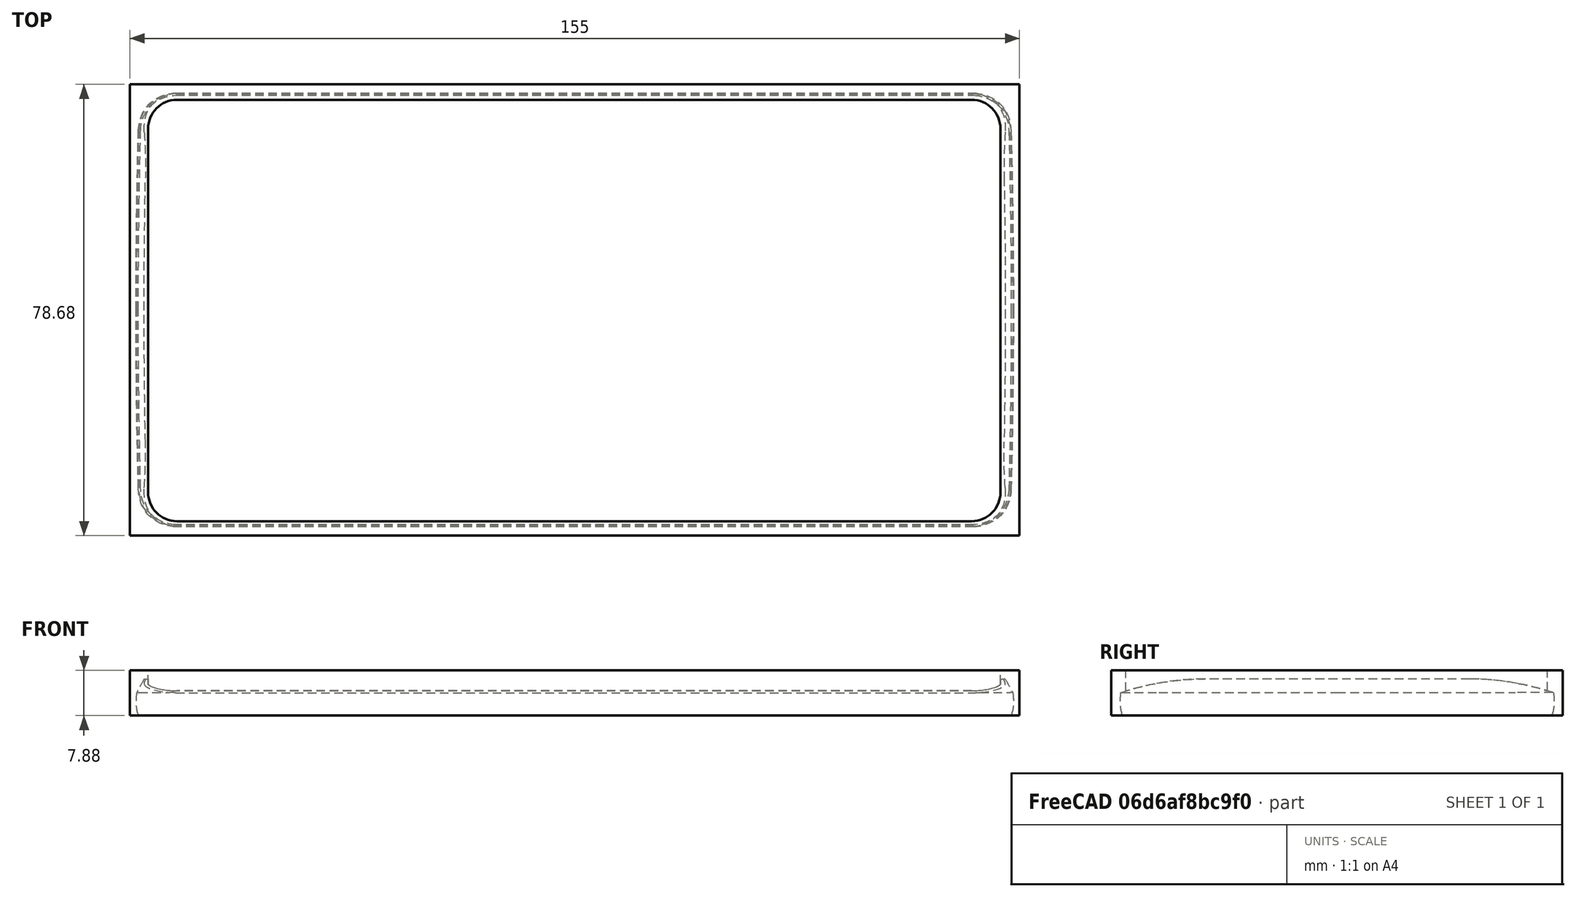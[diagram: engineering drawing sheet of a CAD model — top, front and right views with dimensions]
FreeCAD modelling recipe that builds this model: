
FCSTD DOCUMENT  (FreeCAD 0.18R13728 (Git))
Label: test109_opcase
License: All rights reserved
LicenseURL: http://en.wikipedia.org/wiki/All_rights_reserved
objects: Sketcher::SketchObject×2, Part::Extrusion×2, Part::Cut×2, Part::Feature×1, Mesh::Feature×1
note: 7 computed .brp shape members not serialized (recipe doc carries the construction recipe); baked Part::Feature solids carry a one-line shape summary decoded from their .brp

FEATURE [Sketcher::SketchObject] Sketch001
  MapMode = 5
  Placement = pos=(0,0,0) rot=(-0.57735,0.57735,0.57735;4.18879rad)
  sketch-geometry (16):
    g0: LineSegment [constr] StartX=-75.75 StartY=7.75 StartZ=0 EndX=0 EndY=7.75 EndZ=0
    g1: LineSegment [constr] StartX=0 StartY=7.75 StartZ=0 EndX=0 EndY=0 EndZ=0
    g2: LineSegment [constr] StartX=0 StartY=0 StartZ=0 EndX=-75.75 EndY=0 EndZ=0
    g3: LineSegment [constr] StartX=-75.75 StartY=0 StartZ=0 EndX=-75.75 EndY=7.75 EndZ=0
    g4: LineSegment [constr] StartX=-75.75 StartY=9.25 StartZ=0 EndX=0 EndY=9.25 EndZ=0
    g5: LineSegment [constr] StartX=1.5 StartY=7.75 StartZ=0 EndX=1.5 EndY=0 EndZ=0
    g6: LineSegment [constr] StartX=0 StartY=-1.5 StartZ=0 EndX=-75.75 EndY=-1.5 EndZ=0
    g7: LineSegment [constr] StartX=-77.25 StartY=0 StartZ=0 EndX=-77.25 EndY=7.75 EndZ=0
    g8: ArcOfCircle [constr] CenterX=0 CenterY=7.75 CenterZ=0 NormalX=0 NormalY=0 NormalZ=1 AngleXU=0 Radius=1.5 StartAngle=0 EndAngle=1.5708
    g9: ArcOfCircle [constr] CenterX=0 CenterY=0 CenterZ=0 NormalX=0 NormalY=0 NormalZ=1 AngleXU=0 Radius=1.5 StartAngle=4.71239 EndAngle=6.28319
    g10: ArcOfCircle [constr] CenterX=-75.75 CenterY=0 CenterZ=0 NormalX=0 NormalY=0 NormalZ=1 AngleXU=0 Radius=1.5 StartAngle=3.14159 EndAngle=4.71239
    g11: ArcOfCircle [constr] CenterX=-75.75 CenterY=7.75 CenterZ=0 NormalX=0 NormalY=0 NormalZ=1 AngleXU=0 Radius=1.5 StartAngle=1.5708 EndAngle=3.14159
    g12: LineSegment StartX=-77.2083 StartY=9.25 StartZ=0 EndX=1.47494 EndY=9.25 EndZ=0
    g13: LineSegment StartX=1.47494 StartY=9.25 StartZ=0 EndX=1.47494 EndY=1.36886 EndZ=0
    g14: LineSegment StartX=1.47494 StartY=1.36886 StartZ=0 EndX=-77.2083 EndY=1.36886 EndZ=0
    g15: LineSegment StartX=-77.2083 StartY=1.36886 StartZ=0 EndX=-77.2083 EndY=9.25 EndZ=0
  constraints (38):
    c: Coincident(g0,g1)
    c: Coincident(g1,g2)
    c: Coincident(g2,g3)
    c: Coincident(g3,g0)
    c: Horizontal(g0)
    c: Horizontal(g2)
    c: Vertical(g1)
    c: Vertical(g3)
    c: Coincident(g1,g-1)
    c: Horizontal(g4)
    c: Horizontal(g6)
    c: Vertical(g5)
    c: Vertical(g7)
    c: Tangent(g4,g8) = 1.5708
    c: Tangent(g5,g8) = 1.5708
    c: Tangent(g5,g9) = 1.5708
    c: Tangent(g6,g9) = 1.5708
    c: Tangent(g6,g10) = 1.5708
    c: Tangent(g7,g10) = 1.5708
    c: Tangent(g7,g11) = 1.5708
    c: Tangent(g4,g11) = 1.5708
    c: Radius(g11) = 1.5
    c: Equal(g11,g8)
    c: Equal(g11,g9)
    c: Equal(g11,g10)
    c: Coincident(g9,g-1)
    c: Coincident(g0,g11)
    c: PointOnObject(g12,g4)
    c: Horizontal(g12)
    c: Coincident(g12,g13)
    c: Vertical(g13)
    c: Coincident(g13,g14)
    c: Horizontal(g14)
    c: Coincident(g14,g15)
    c: Coincident(g15,g12)
    c: Vertical(g15)
    c: DistanceX(g0) = -75.75
    c: DistanceY(g0) = 7.75
FEATURE [Part::Extrusion] Extrude
  Base = -> Sketch001
  Dir = (-1,0,0)
  DirMode = 2
  FaceMakerClass = Part::FaceMakerBullseye
  LengthFwd = 155
  LengthRev = 0
  Placement = pos=(-1,0,0) rot=(0,0,1;0rad)
  Reversed = true
  Solid = true
  Symmetric = false
FEATURE [Part::Feature] test108_op3base
  shape: bbox 153.3 x 76.01 x 7.75 mm, 74 faces (baked)
FEATURE [Part::Cut] Cut
  Base = -> Extrude
  Tool = -> test108_op3base
FEATURE [Sketcher::SketchObject] Sketch
  MapMode = 5
  Placement = pos=(0,0,1.36886) rot=(1,0,0;3.14159rad)
  Support = -> [Cut]
  sketch-geometry (8):
    g0: LineSegment StartX=7.16177 StartY=-1.04562 StartZ=0 EndX=145.686 EndY=-1.04562 EndZ=0
    g1: LineSegment StartX=150.686 StartY=-6.04562 StartZ=0 EndX=150.686 EndY=-69.4963 EndZ=0
    g2: LineSegment StartX=145.686 StartY=-74.4963 StartZ=0 EndX=7.16177 EndY=-74.4963 EndZ=0
    g3: LineSegment StartX=2.16177 StartY=-69.4963 StartZ=0 EndX=2.16177 EndY=-6.04562 EndZ=0
    g4: ArcOfCircle CenterX=7.16177 CenterY=-6.04562 CenterZ=0 NormalX=0 NormalY=0 NormalZ=1 AngleXU=0 Radius=5 StartAngle=1.5708 EndAngle=3.14159
    g5: ArcOfCircle CenterX=145.686 CenterY=-6.04562 CenterZ=0 NormalX=0 NormalY=0 NormalZ=1 AngleXU=0 Radius=5 StartAngle=0 EndAngle=1.5708
    g6: ArcOfCircle CenterX=145.686 CenterY=-69.4963 CenterZ=0 NormalX=0 NormalY=0 NormalZ=1 AngleXU=0 Radius=5 StartAngle=4.71239 EndAngle=6.28319
    g7: ArcOfCircle CenterX=7.16177 CenterY=-69.4963 CenterZ=0 NormalX=0 NormalY=0 NormalZ=1 AngleXU=0 Radius=5 StartAngle=3.14159 EndAngle=4.71239
  constraints (16):
    c: Horizontal(g0)
    c: Horizontal(g2)
    c: Vertical(g1)
    c: Vertical(g3)
    c: Tangent(g3,g4) = 1.5708
    c: Tangent(g0,g4) = 1.5708
    c: Tangent(g0,g5) = 1.5708
    c: Tangent(g1,g5) = 1.5708
    c: Tangent(g1,g6) = 1.5708
    c: Tangent(g2,g6) = 1.5708
    c: Tangent(g2,g7) = 1.5708
    c: Tangent(g3,g7) = 1.5708
    c: Radius(g7) = 5
    c: Equal(g7,g4)
    c: Equal(g7,g5)
    c: Equal(g7,g6)
FEATURE [Part::Extrusion] Extrude001
  Base = -> Sketch
  Dir = (0,0,-1)
  DirMode = 2
  FaceMakerClass = Part::FaceMakerBullseye
  LengthFwd = 10
  LengthRev = 0
  Reversed = true
  Solid = true
  Symmetric = false
FEATURE [Part::Cut] Cut001
  Base = -> Cut
  Tool = -> Extrude001
FEATURE [Mesh::Feature] Mesh  label="Cut001 (Meshed)"
